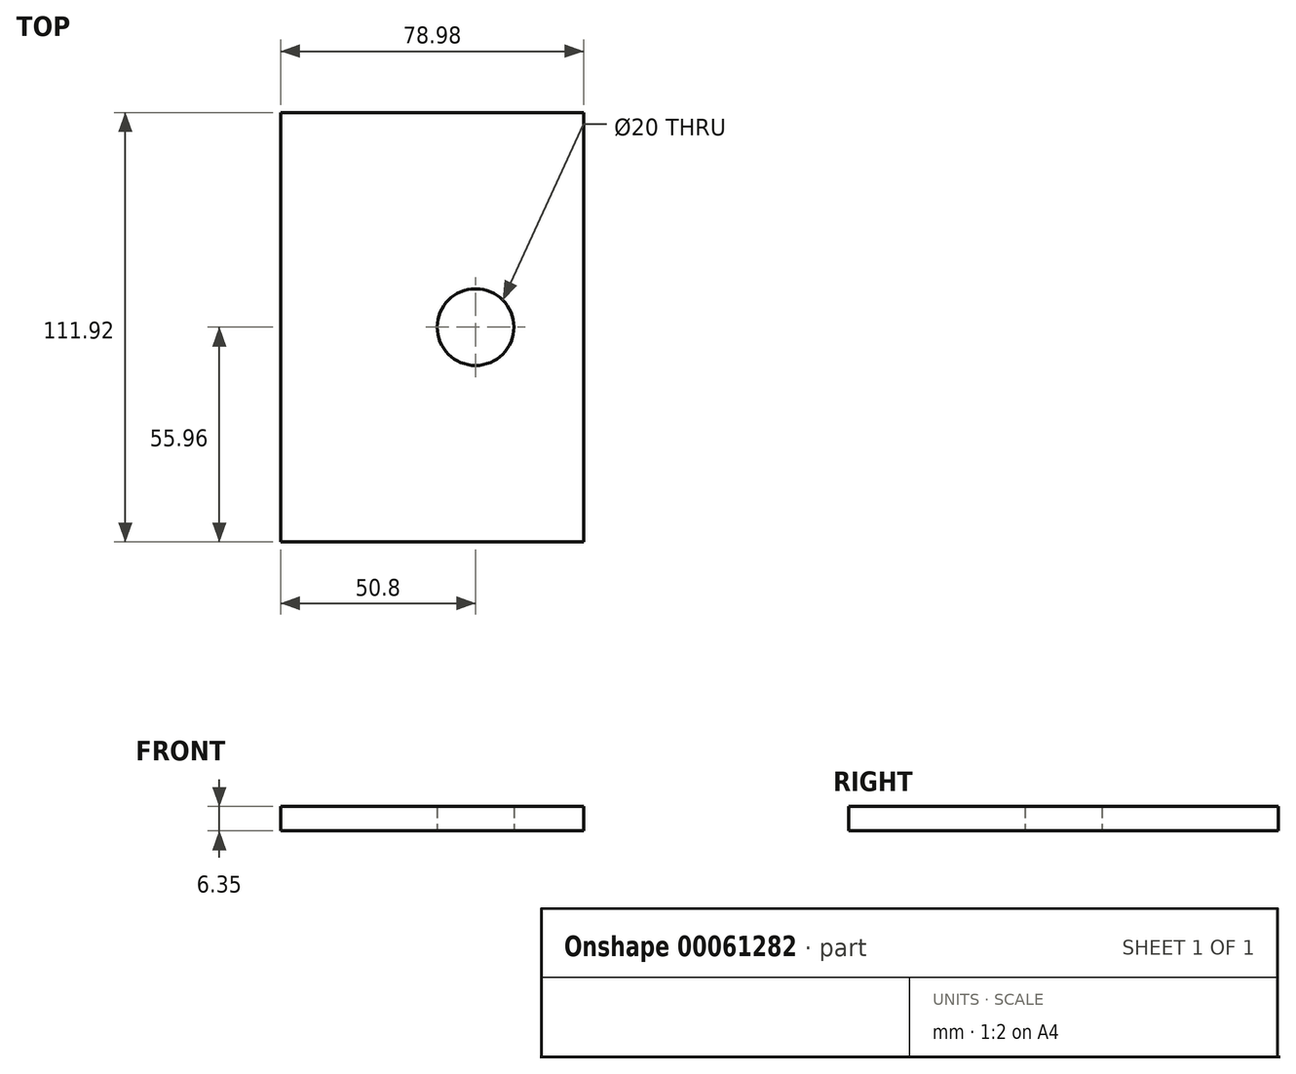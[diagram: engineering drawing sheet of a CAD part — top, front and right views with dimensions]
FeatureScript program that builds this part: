
annotation { "Feature Type Name" : "Feature", "Feature Type Description" : "" }
export const myFeature = defineFeature(function(context is Context, id is Id, definition is map)
    precondition{}
    {
        {
            var Q0;
            Q0=qCreatedBy(makeId("Top.planeOp"),FACE);
            var sketch = newSketch(context, id + "F0", { "sketchPlane" : qUnion([Q0])});
            skLineSegment(sketch, "E0.rect.bottom", {"start": v(50.8, 55.96) * mm, "end": v(-50.8, 55.96) * mm});
            skLineSegment(sketch, "E0.rect.top", {"start": v(50.8, -55.96) * mm, "end": v(-50.8, -55.96) * mm});
            skLineSegment(sketch, "E0.rect.left", {"start": v(50.8, 55.96) * mm, "end": v(50.8, -55.96) * mm});
            skLineSegment(sketch, "E0.rect.right", {"start": v(-50.8, 55.96) * mm, "end": v(-50.8, -55.96) * mm, "construction": true});
            skPoint(sketch, "E0.rect.middle", {"position": v(0, 0) * mm});
            skCircle(sketch, "E1", {"center": v(0, 0) * mm, "radius": 10 * mm});
            skLineSegment(sketch, "E2.bottom", {"start": v(-50.8, -55.96) * mm, "end": v(-152.4, -55.96) * mm});
            skLineSegment(sketch, "E2.top", {"start": v(-50.8, 55.96) * mm, "end": v(-152.4, 55.96) * mm});
            skLineSegment(sketch, "E2.left", {"start": v(-50.8, -55.96) * mm, "end": v(-50.8, 55.96) * mm, "construction": true});
            skLineSegment(sketch, "E2.right", {"start": v(-152.4, -55.96) * mm, "end": v(-152.4, 55.96) * mm});
            skCircle(sketch, "E3", {"center": v(-101.6, 0) * mm, "radius": 10 * mm});
            skPoint(sketch, "E3.centerSnap0", {"position": v(-101.6, 55.96) * mm});
            skSolve(sketch);
        }
        {
            var Q0;
            Q0=makeQuery(id+"F0.imprint","IMPRINT",FACE,{"disambiguationData":[TD([[makeQuery(id+"F0.imprint","IMPRINT",EDGE,{"derivedFrom":sQuery(id+"F0.wireOp",EDGE,"E0.rect.bottom")}),1.0]])]});
            extrude(context, id + "F1", {"entities" : qUnion([Q0]), "depth" : 6.35 * mm});
        }
        {
            var Q0;
            Q0=makeQuery(id+"F1.opExtrude","CAP_FACE",FACE,{"disambiguationData":[OSD([sQuery(id+"F0.wireOp",EDGE,"E0.rect.bottom"),sQuery(id+"F0.wireOp",EDGE,"E0.rect.top"),sQuery(id+"F0.wireOp",EDGE,"E0.rect.left"),sQuery(id+"F0.wireOp",EDGE,"E1"),sQuery(id+"F0.wireOp",EDGE,"E2.bottom"),sQuery(id+"F0.wireOp",EDGE,"E2.top"),sQuery(id+"F0.wireOp",EDGE,"E2.right"),sQuery(id+"F0.wireOp",EDGE,"E3")])],"isStart":false});
            var sketch = newSketch(context, id + "F2", { "sketchPlane" : qUnion([Q0])});
            skLineSegment(sketch, "E4", {"start": v(-73.42, 55.96) * mm, "end": v(-73.42, -55.96) * mm});
            skCircle(sketch, "E5.0", {"center": v(-101.6, 0) * mm, "radius": 10 * mm});
            skCircle(sketch, "E6.0", {"center": v(0, 0) * mm, "radius": 10 * mm});
            skLineSegment(sketch, "E7", {"start": v(-152.4, 55.96) * mm, "end": v(-152.4, 55.96) * mm});
            skLineSegment(sketch, "E8", {"start": v(50.8, 55.96) * mm, "end": v(50.8, 55.96) * mm});
            skLineSegment(sketch, "E9", {"start": v(-73.42, 55.96) * mm, "end": v(-73.42, 55.96) * mm});
            skSolve(sketch);
        }
        {
            var Q0;
            {var subQ0=sQuery(id+"F2.wireOp",EDGE,"E8");Q0=makeQuery(id+"F2.imprint","IMPRINT",FACE,{"disambiguationData":[TD([[makeQuery(id+"F2.imprint","IMPRINT",EDGE,{"derivedFrom":subQ0}),-1.0]])]});}
            var Q1;
            {var subQ2=sQuery(id+"F2.wireOp",EDGE,"E4");Q1=makeQuery(id+"F2.imprint","IMPRINT",FACE,{"disambiguationData":[TD([[makeQuery(id+"F2.imprint","IMPRINT",EDGE,{"derivedFrom":subQ2}),1.0]])]});}
            extrude(context, id + "F3", {"entities" : qUnion([Q0, Q1]), "operationType" : NewBodyOperationType.REMOVE, "endBound" : BoundingType.THROUGH_ALL, "oppositeDirection" : true, "depth" : 25.4 * mm});
        }
    });
